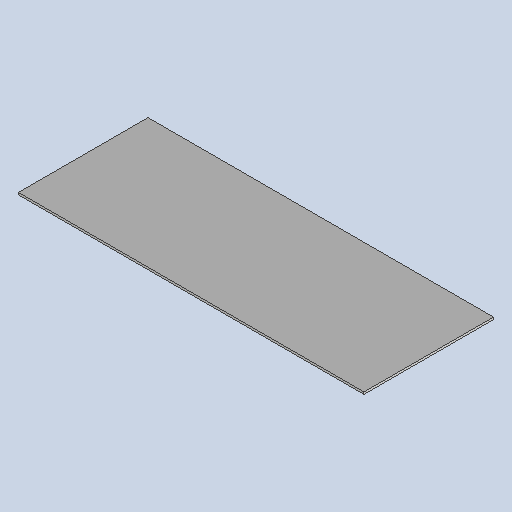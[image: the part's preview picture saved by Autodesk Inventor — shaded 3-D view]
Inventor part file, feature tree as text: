
AUTODESK INVENTOR PART (.ipt)
format: ipt  version: 2025 (Build 290162010, 162A)  size: 239,104 bytes
history: native  units: mm
features: other x4, sketch x2, sheet_metal_op x1
ambient origin geometry x8: Origin, YZ Plane, XZ Plane, XY Plane, X Axis, Y Axis, Z Axis, Center Point
bodies: Solid1 (feature_tree)
feature tree (7):
  sheet_metal_op  "Face1"
  other  "Mark1"
  other  "A-Side Definition"
  sketch  "Sketch1"  dims[d0=480.0mm]
  other  "Plate1"
  sketch  "Sketch2"  dims[d1=180.0mm d2=3.0mm d6=200.0mm d7=20.0mm d8=20.0mm d9=20.0mm]
  other  "Definition1"
